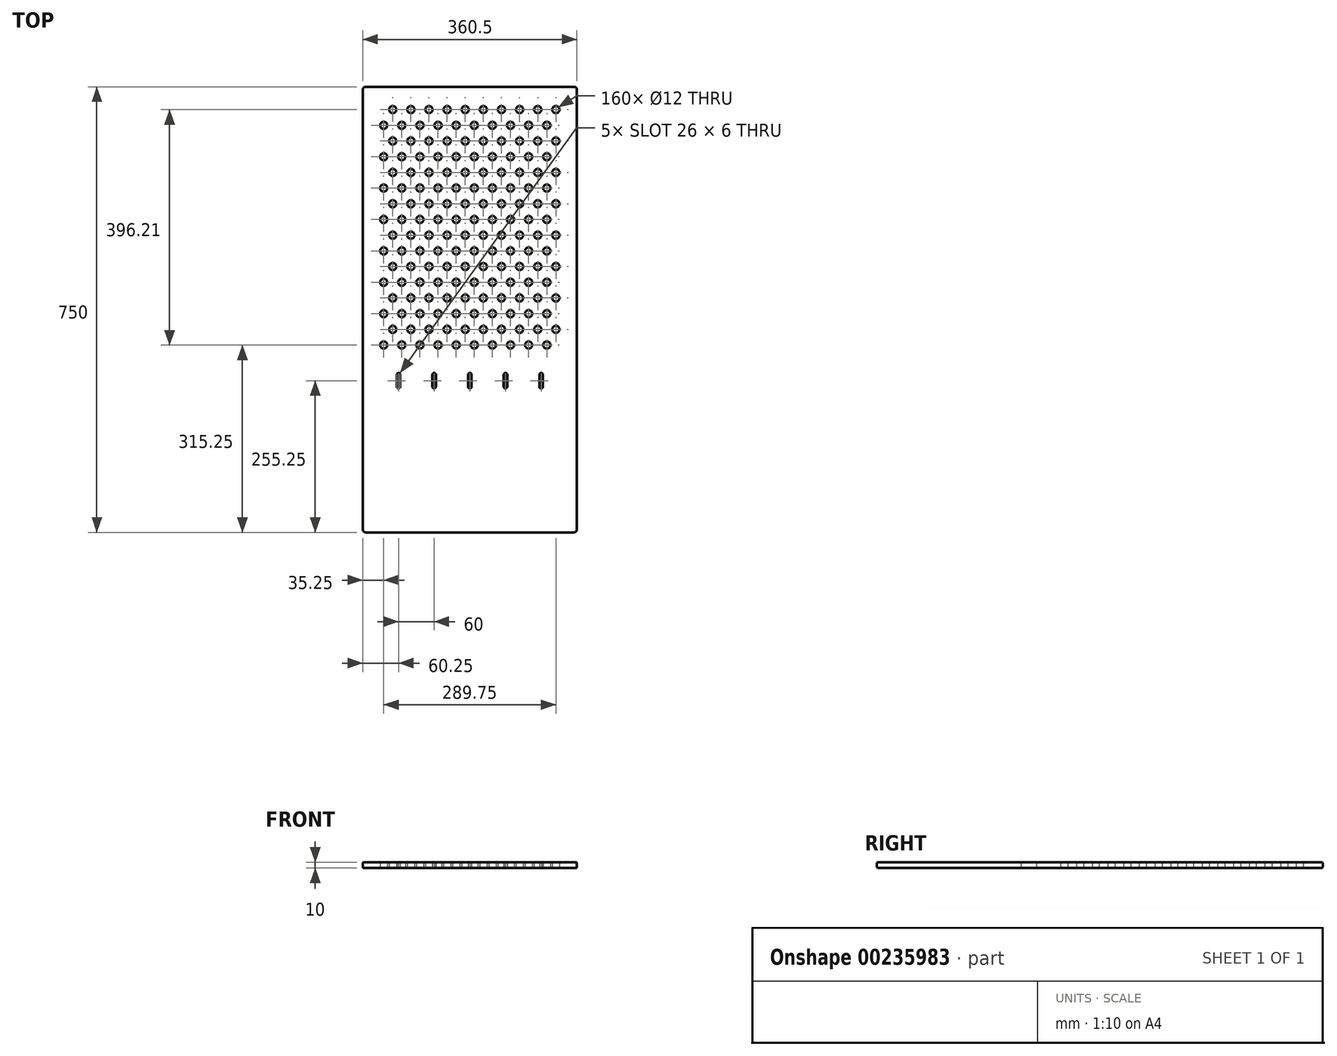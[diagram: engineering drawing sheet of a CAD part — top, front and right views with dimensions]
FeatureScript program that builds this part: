
annotation { "Feature Type Name" : "Feature", "Feature Type Description" : "" }
export const myFeature = defineFeature(function(context is Context, id is Id, definition is map)
    precondition{}
    {
        {
            var Q0;
            Q0=qCreatedBy(makeId("Top.planeOp"),FACE);
            var sketch = newSketch(context, id + "F0", { "sketchPlane" : qUnion([Q0])});
            skCircle(sketch, "E0", {"center": v(0, 0) * mm, "radius": 15.25 * mm, "construction": true});
            skLineSegment(sketch, "E1", {"start": v(-15.25, 59.88) * mm, "end": v(-15.25, -39.27) * mm, "construction": true});
            skLineSegment(sketch, "E2", {"start": v(-42.71, -15.25) * mm, "end": v(49.2, -15.25) * mm, "construction": true});
            skLineSegment(sketch, "E3.direction1", {"start": v(0, 0) * mm, "end": v(30.5, 0) * mm, "construction": true});
            skLineSegment(sketch, "E3.direction2", {"start": v(0, 0) * mm, "end": v(0, 30.5) * mm, "construction": true});
            skCircle(sketch, "E4", {"center": v(0, 0) * mm, "radius": 6 * mm});
            skCircle(sketch, "E5.0.1.0", {"center": v(0, 52.83) * mm, "radius": 6 * mm});
            skCircle(sketch, "E5.0.2.0", {"center": v(0, 105.66) * mm, "radius": 6 * mm});
            skCircle(sketch, "E5.0.3.0", {"center": v(0, 158.48) * mm, "radius": 6 * mm});
            skCircle(sketch, "E5.0.4.0", {"center": v(0, 211.31) * mm, "radius": 6 * mm});
            skCircle(sketch, "E5.0.5.0", {"center": v(0, 264.14) * mm, "radius": 6 * mm});
            skCircle(sketch, "E5.1.0.0", {"center": v(30.5, 0) * mm, "radius": 6 * mm});
            skCircle(sketch, "E5.1.1.0", {"center": v(30.5, 52.83) * mm, "radius": 6 * mm});
            skCircle(sketch, "E5.1.2.0", {"center": v(30.5, 105.66) * mm, "radius": 6 * mm});
            skCircle(sketch, "E5.1.3.0", {"center": v(30.5, 158.48) * mm, "radius": 6 * mm});
            skCircle(sketch, "E5.1.4.0", {"center": v(30.5, 211.31) * mm, "radius": 6 * mm});
            skCircle(sketch, "E5.1.5.0", {"center": v(30.5, 264.14) * mm, "radius": 6 * mm});
            skCircle(sketch, "E5.2.0.0", {"center": v(61, 0) * mm, "radius": 6 * mm});
            skCircle(sketch, "E5.2.1.0", {"center": v(61, 52.83) * mm, "radius": 6 * mm});
            skCircle(sketch, "E5.2.2.0", {"center": v(61, 105.66) * mm, "radius": 6 * mm});
            skCircle(sketch, "E5.2.3.0", {"center": v(61, 158.48) * mm, "radius": 6 * mm});
            skCircle(sketch, "E5.2.4.0", {"center": v(61, 211.31) * mm, "radius": 6 * mm});
            skCircle(sketch, "E5.2.5.0", {"center": v(61, 264.14) * mm, "radius": 6 * mm});
            skCircle(sketch, "E5.3.0.0", {"center": v(91.5, 0) * mm, "radius": 6 * mm});
            skCircle(sketch, "E5.3.1.0", {"center": v(91.5, 52.83) * mm, "radius": 6 * mm});
            skCircle(sketch, "E5.3.2.0", {"center": v(91.5, 105.66) * mm, "radius": 6 * mm});
            skCircle(sketch, "E5.3.3.0", {"center": v(91.5, 158.48) * mm, "radius": 6 * mm});
            skCircle(sketch, "E5.3.4.0", {"center": v(91.5, 211.31) * mm, "radius": 6 * mm});
            skCircle(sketch, "E5.3.5.0", {"center": v(91.5, 264.14) * mm, "radius": 6 * mm});
            skCircle(sketch, "E5.4.0.0", {"center": v(122, 0) * mm, "radius": 6 * mm});
            skCircle(sketch, "E5.4.1.0", {"center": v(122, 52.83) * mm, "radius": 6 * mm});
            skCircle(sketch, "E5.4.2.0", {"center": v(122, 105.66) * mm, "radius": 6 * mm});
            skCircle(sketch, "E5.4.3.0", {"center": v(122, 158.48) * mm, "radius": 6 * mm});
            skCircle(sketch, "E5.4.4.0", {"center": v(122, 211.31) * mm, "radius": 6 * mm});
            skCircle(sketch, "E5.4.5.0", {"center": v(122, 264.14) * mm, "radius": 6 * mm});
            skCircle(sketch, "E5.5.0.0", {"center": v(152.5, 0) * mm, "radius": 6 * mm});
            skCircle(sketch, "E5.5.1.0", {"center": v(152.5, 52.83) * mm, "radius": 6 * mm});
            skCircle(sketch, "E5.5.2.0", {"center": v(152.5, 105.66) * mm, "radius": 6 * mm});
            skCircle(sketch, "E5.5.3.0", {"center": v(152.5, 158.48) * mm, "radius": 6 * mm});
            skCircle(sketch, "E5.5.4.0", {"center": v(152.5, 211.31) * mm, "radius": 6 * mm});
            skCircle(sketch, "E5.5.5.0", {"center": v(152.5, 264.14) * mm, "radius": 6 * mm});
            skCircle(sketch, "E5.6.0.0", {"center": v(183, 0) * mm, "radius": 6 * mm});
            skCircle(sketch, "E5.6.1.0", {"center": v(183, 52.83) * mm, "radius": 6 * mm});
            skCircle(sketch, "E5.6.2.0", {"center": v(183, 105.66) * mm, "radius": 6 * mm});
            skCircle(sketch, "E5.6.3.0", {"center": v(183, 158.48) * mm, "radius": 6 * mm});
            skCircle(sketch, "E5.6.4.0", {"center": v(183, 211.31) * mm, "radius": 6 * mm});
            skCircle(sketch, "E5.6.5.0", {"center": v(183, 264.14) * mm, "radius": 6 * mm});
            skLineSegment(sketch, "E5.direction2", {"start": v(0, 0) * mm, "end": v(0, 52.83) * mm, "construction": true});
            skLineSegment(sketch, "E6", {"start": v(-15.25, -15.25) * mm, "end": v(305.25, -15.25) * mm, "construction": true});
            skPoint(sketch, "E6.endSnap0", {"position": v(3.24, -15.25) * mm});
            skLineSegment(sketch, "E7", {"start": v(305.25, -15.25) * mm, "end": v(305.25, 414.75) * mm, "construction": true});
            skLineSegment(sketch, "E8", {"start": v(305.25, 414.75) * mm, "end": v(-15.25, 414.75) * mm, "construction": true});
            skLineSegment(sketch, "E9", {"start": v(-15.25, 414.75) * mm, "end": v(-15.25, -15.25) * mm, "construction": true});
            skCircle(sketch, "E10.0.7.0", {"center": v(213.5, 0) * mm, "radius": 6 * mm});
            skCircle(sketch, "E10.0.7.1", {"center": v(213.5, 52.83) * mm, "radius": 6 * mm});
            skCircle(sketch, "E10.0.7.2", {"center": v(213.5, 105.66) * mm, "radius": 6 * mm});
            skCircle(sketch, "E10.0.7.3", {"center": v(213.5, 158.48) * mm, "radius": 6 * mm});
            skCircle(sketch, "E10.0.7.4", {"center": v(213.5, 211.31) * mm, "radius": 6 * mm});
            skCircle(sketch, "E10.0.7.5", {"center": v(213.5, 264.14) * mm, "radius": 6 * mm});
            skCircle(sketch, "E10.0.8.0", {"center": v(244, 0) * mm, "radius": 6 * mm});
            skCircle(sketch, "E10.0.8.1", {"center": v(244, 52.83) * mm, "radius": 6 * mm});
            skCircle(sketch, "E10.0.8.2", {"center": v(244, 105.66) * mm, "radius": 6 * mm});
            skCircle(sketch, "E10.0.8.3", {"center": v(244, 158.48) * mm, "radius": 6 * mm});
            skCircle(sketch, "E10.0.8.4", {"center": v(244, 211.31) * mm, "radius": 6 * mm});
            skCircle(sketch, "E10.0.8.5", {"center": v(244, 264.14) * mm, "radius": 6 * mm});
            skCircle(sketch, "E11.0.9.0", {"center": v(274.5, 0) * mm, "radius": 6 * mm});
            skCircle(sketch, "E11.0.9.1", {"center": v(274.5, 52.83) * mm, "radius": 6 * mm});
            skCircle(sketch, "E11.0.9.2", {"center": v(274.5, 105.66) * mm, "radius": 6 * mm});
            skCircle(sketch, "E11.0.9.3", {"center": v(274.5, 158.48) * mm, "radius": 6 * mm});
            skCircle(sketch, "E11.0.9.4", {"center": v(274.5, 211.31) * mm, "radius": 6 * mm});
            skCircle(sketch, "E11.0.9.5", {"center": v(274.5, 264.14) * mm, "radius": 6 * mm});
            skLineSegment(sketch, "E12", {"start": v(-35.25, 434.75) * mm, "end": v(325.25, 434.75) * mm});
            skLineSegment(sketch, "E13", {"start": v(325.25, 434.75) * mm, "end": v(325.25, -315.25) * mm});
            skLineSegment(sketch, "E14", {"start": v(325.25, -315.25) * mm, "end": v(-35.25, -315.25) * mm});
            skLineSegment(sketch, "E15", {"start": v(-35.25, -315.25) * mm, "end": v(-35.25, 434.75) * mm});
            skCircle(sketch, "E16", {"center": v(30.5, 0) * mm, "radius": 15.25 * mm, "construction": true});
            skCircle(sketch, "E17", {"center": v(15.25, 26.41) * mm, "radius": 15.25 * mm, "construction": true});
            skCircle(sketch, "E18", {"center": v(0, 52.83) * mm, "radius": 15.25 * mm, "construction": true});
            skCircle(sketch, "E19.0.0.6", {"center": v(0, 316.97) * mm, "radius": 6 * mm});
            skCircle(sketch, "E19.0.0.7", {"center": v(0, 369.8) * mm, "radius": 6 * mm});
            skCircle(sketch, "E19.0.1.6", {"center": v(30.5, 316.97) * mm, "radius": 6 * mm});
            skCircle(sketch, "E19.0.1.7", {"center": v(30.5, 369.8) * mm, "radius": 6 * mm});
            skCircle(sketch, "E19.0.2.6", {"center": v(61, 316.97) * mm, "radius": 6 * mm});
            skCircle(sketch, "E19.0.2.7", {"center": v(61, 369.8) * mm, "radius": 6 * mm});
            skCircle(sketch, "E19.0.3.6", {"center": v(91.5, 316.97) * mm, "radius": 6 * mm});
            skCircle(sketch, "E19.0.3.7", {"center": v(91.5, 369.8) * mm, "radius": 6 * mm});
            skCircle(sketch, "E19.0.4.6", {"center": v(122, 316.97) * mm, "radius": 6 * mm});
            skCircle(sketch, "E19.0.4.7", {"center": v(122, 369.8) * mm, "radius": 6 * mm});
            skCircle(sketch, "E19.0.5.6", {"center": v(152.5, 316.97) * mm, "radius": 6 * mm});
            skCircle(sketch, "E19.0.5.7", {"center": v(152.5, 369.8) * mm, "radius": 6 * mm});
            skCircle(sketch, "E19.0.6.6", {"center": v(183, 316.97) * mm, "radius": 6 * mm});
            skCircle(sketch, "E19.0.6.7", {"center": v(183, 369.8) * mm, "radius": 6 * mm});
            skCircle(sketch, "E19.0.7.6", {"center": v(213.5, 316.97) * mm, "radius": 6 * mm});
            skCircle(sketch, "E19.0.7.7", {"center": v(213.5, 369.8) * mm, "radius": 6 * mm});
            skCircle(sketch, "E19.0.8.6", {"center": v(244, 316.97) * mm, "radius": 6 * mm});
            skCircle(sketch, "E19.0.8.7", {"center": v(244, 369.8) * mm, "radius": 6 * mm});
            skCircle(sketch, "E19.0.9.6", {"center": v(274.5, 316.97) * mm, "radius": 6 * mm});
            skCircle(sketch, "E19.0.9.7", {"center": v(274.5, 369.8) * mm, "radius": 6 * mm});
            skCircle(sketch, "E20", {"center": v(15.25, 26.41) * mm, "radius": 6 * mm});
            skCircle(sketch, "E21.0.1.0", {"center": v(15.25, 79.24) * mm, "radius": 6 * mm});
            skCircle(sketch, "E21.0.2.0", {"center": v(15.25, 132.07) * mm, "radius": 6 * mm});
            skCircle(sketch, "E21.0.3.0", {"center": v(15.25, 184.9) * mm, "radius": 6 * mm});
            skCircle(sketch, "E21.0.4.0", {"center": v(15.25, 237.73) * mm, "radius": 6 * mm});
            skCircle(sketch, "E21.0.5.0", {"center": v(15.25, 290.55) * mm, "radius": 6 * mm});
            skCircle(sketch, "E21.0.6.0", {"center": v(15.25, 343.38) * mm, "radius": 6 * mm});
            skCircle(sketch, "E21.1.0.0", {"center": v(45.75, 26.41) * mm, "radius": 6 * mm});
            skCircle(sketch, "E21.1.1.0", {"center": v(45.75, 79.24) * mm, "radius": 6 * mm});
            skCircle(sketch, "E21.1.2.0", {"center": v(45.75, 132.07) * mm, "radius": 6 * mm});
            skCircle(sketch, "E21.1.3.0", {"center": v(45.75, 184.9) * mm, "radius": 6 * mm});
            skCircle(sketch, "E21.1.4.0", {"center": v(45.75, 237.73) * mm, "radius": 6 * mm});
            skCircle(sketch, "E21.1.5.0", {"center": v(45.75, 290.55) * mm, "radius": 6 * mm});
            skCircle(sketch, "E21.1.6.0", {"center": v(45.75, 343.38) * mm, "radius": 6 * mm});
            skCircle(sketch, "E21.2.0.0", {"center": v(76.25, 26.41) * mm, "radius": 6 * mm});
            skCircle(sketch, "E21.2.1.0", {"center": v(76.25, 79.24) * mm, "radius": 6 * mm});
            skCircle(sketch, "E21.2.2.0", {"center": v(76.25, 132.07) * mm, "radius": 6 * mm});
            skCircle(sketch, "E21.2.3.0", {"center": v(76.25, 184.9) * mm, "radius": 6 * mm});
            skCircle(sketch, "E21.2.4.0", {"center": v(76.25, 237.73) * mm, "radius": 6 * mm});
            skCircle(sketch, "E21.2.5.0", {"center": v(76.25, 290.55) * mm, "radius": 6 * mm});
            skCircle(sketch, "E21.2.6.0", {"center": v(76.25, 343.38) * mm, "radius": 6 * mm});
            skCircle(sketch, "E21.3.0.0", {"center": v(106.75, 26.41) * mm, "radius": 6 * mm});
            skCircle(sketch, "E21.3.1.0", {"center": v(106.75, 79.24) * mm, "radius": 6 * mm});
            skCircle(sketch, "E21.3.2.0", {"center": v(106.75, 132.07) * mm, "radius": 6 * mm});
            skCircle(sketch, "E21.3.3.0", {"center": v(106.75, 184.9) * mm, "radius": 6 * mm});
            skCircle(sketch, "E21.3.4.0", {"center": v(106.75, 237.73) * mm, "radius": 6 * mm});
            skCircle(sketch, "E21.3.5.0", {"center": v(106.75, 290.55) * mm, "radius": 6 * mm});
            skCircle(sketch, "E21.3.6.0", {"center": v(106.75, 343.38) * mm, "radius": 6 * mm});
            skCircle(sketch, "E21.4.0.0", {"center": v(137.25, 26.41) * mm, "radius": 6 * mm});
            skCircle(sketch, "E21.4.1.0", {"center": v(137.25, 79.24) * mm, "radius": 6 * mm});
            skCircle(sketch, "E21.4.2.0", {"center": v(137.25, 132.07) * mm, "radius": 6 * mm});
            skCircle(sketch, "E21.4.3.0", {"center": v(137.25, 184.9) * mm, "radius": 6 * mm});
            skCircle(sketch, "E21.4.4.0", {"center": v(137.25, 237.73) * mm, "radius": 6 * mm});
            skCircle(sketch, "E21.4.5.0", {"center": v(137.25, 290.55) * mm, "radius": 6 * mm});
            skCircle(sketch, "E21.4.6.0", {"center": v(137.25, 343.38) * mm, "radius": 6 * mm});
            skCircle(sketch, "E21.5.0.0", {"center": v(167.75, 26.41) * mm, "radius": 6 * mm});
            skCircle(sketch, "E21.5.1.0", {"center": v(167.75, 79.24) * mm, "radius": 6 * mm});
            skCircle(sketch, "E21.5.2.0", {"center": v(167.75, 132.07) * mm, "radius": 6 * mm});
            skCircle(sketch, "E21.5.3.0", {"center": v(167.75, 184.9) * mm, "radius": 6 * mm});
            skCircle(sketch, "E21.5.4.0", {"center": v(167.75, 237.73) * mm, "radius": 6 * mm});
            skCircle(sketch, "E21.5.5.0", {"center": v(167.75, 290.55) * mm, "radius": 6 * mm});
            skCircle(sketch, "E21.5.6.0", {"center": v(167.75, 343.38) * mm, "radius": 6 * mm});
            skCircle(sketch, "E21.6.0.0", {"center": v(198.25, 26.41) * mm, "radius": 6 * mm});
            skCircle(sketch, "E21.6.1.0", {"center": v(198.25, 79.24) * mm, "radius": 6 * mm});
            skCircle(sketch, "E21.6.2.0", {"center": v(198.25, 132.07) * mm, "radius": 6 * mm});
            skCircle(sketch, "E21.6.3.0", {"center": v(198.25, 184.9) * mm, "radius": 6 * mm});
            skCircle(sketch, "E21.6.4.0", {"center": v(198.25, 237.73) * mm, "radius": 6 * mm});
            skCircle(sketch, "E21.6.5.0", {"center": v(198.25, 290.55) * mm, "radius": 6 * mm});
            skCircle(sketch, "E21.6.6.0", {"center": v(198.25, 343.38) * mm, "radius": 6 * mm});
            skCircle(sketch, "E21.7.0.0", {"center": v(228.75, 26.41) * mm, "radius": 6 * mm});
            skCircle(sketch, "E21.7.1.0", {"center": v(228.75, 79.24) * mm, "radius": 6 * mm});
            skCircle(sketch, "E21.7.2.0", {"center": v(228.75, 132.07) * mm, "radius": 6 * mm});
            skCircle(sketch, "E21.7.3.0", {"center": v(228.75, 184.9) * mm, "radius": 6 * mm});
            skCircle(sketch, "E21.7.4.0", {"center": v(228.75, 237.73) * mm, "radius": 6 * mm});
            skCircle(sketch, "E21.7.5.0", {"center": v(228.75, 290.55) * mm, "radius": 6 * mm});
            skCircle(sketch, "E21.7.6.0", {"center": v(228.75, 343.38) * mm, "radius": 6 * mm});
            skCircle(sketch, "E21.8.0.0", {"center": v(259.25, 26.41) * mm, "radius": 6 * mm});
            skCircle(sketch, "E21.8.1.0", {"center": v(259.25, 79.24) * mm, "radius": 6 * mm});
            skCircle(sketch, "E21.8.2.0", {"center": v(259.25, 132.07) * mm, "radius": 6 * mm});
            skCircle(sketch, "E21.8.3.0", {"center": v(259.25, 184.9) * mm, "radius": 6 * mm});
            skCircle(sketch, "E21.8.4.0", {"center": v(259.25, 237.73) * mm, "radius": 6 * mm});
            skCircle(sketch, "E21.8.5.0", {"center": v(259.25, 290.55) * mm, "radius": 6 * mm});
            skCircle(sketch, "E21.8.6.0", {"center": v(259.25, 343.38) * mm, "radius": 6 * mm});
            skCircle(sketch, "E21.9.0.0", {"center": v(289.75, 26.41) * mm, "radius": 6 * mm});
            skCircle(sketch, "E21.9.1.0", {"center": v(289.75, 79.24) * mm, "radius": 6 * mm});
            skCircle(sketch, "E21.9.2.0", {"center": v(289.75, 132.07) * mm, "radius": 6 * mm});
            skCircle(sketch, "E21.9.3.0", {"center": v(289.75, 184.9) * mm, "radius": 6 * mm});
            skCircle(sketch, "E21.9.4.0", {"center": v(289.75, 237.73) * mm, "radius": 6 * mm});
            skCircle(sketch, "E21.9.5.0", {"center": v(289.75, 290.55) * mm, "radius": 6 * mm});
            skCircle(sketch, "E21.9.6.0", {"center": v(289.75, 343.38) * mm, "radius": 6 * mm});
            skLineSegment(sketch, "E21.direction1", {"start": v(15.25, 26.41) * mm, "end": v(45.75, 26.41) * mm, "construction": true});
            skLineSegment(sketch, "E21.direction2", {"start": v(15.25, 26.41) * mm, "end": v(15.25, 79.24) * mm, "construction": true});
            skCircle(sketch, "E22.0.0.7", {"center": v(15.25, 396.2) * mm, "radius": 6 * mm});
            skCircle(sketch, "E22.0.1.7", {"center": v(45.75, 396.2) * mm, "radius": 6 * mm});
            skCircle(sketch, "E22.0.2.7", {"center": v(76.25, 396.2) * mm, "radius": 6 * mm});
            skCircle(sketch, "E22.0.3.7", {"center": v(106.75, 396.2) * mm, "radius": 6 * mm});
            skCircle(sketch, "E22.0.4.7", {"center": v(137.25, 396.2) * mm, "radius": 6 * mm});
            skCircle(sketch, "E22.0.5.7", {"center": v(167.75, 396.2) * mm, "radius": 6 * mm});
            skCircle(sketch, "E22.0.6.7", {"center": v(198.25, 396.2) * mm, "radius": 6 * mm});
            skCircle(sketch, "E22.0.7.7", {"center": v(228.75, 396.2) * mm, "radius": 6 * mm});
            skCircle(sketch, "E22.0.8.7", {"center": v(259.25, 396.2) * mm, "radius": 6 * mm});
            skCircle(sketch, "E22.0.9.7", {"center": v(289.75, 396.2) * mm, "radius": 6 * mm});
            skSolve(sketch);
        }
        {
            var Q0;
            Q0 = qSketchRegion(id + "F0", true);
            extrude(context, id + "F1", {"entities" : qUnion([Q0]), "depth" : 10 * mm});
        }
        {
            var Q0;
            Q0=makeQuery(id+"F0.imprint","IMPRINT",FACE,{"disambiguationData":[TD([[makeQuery(id+"F0.imprint","IMPRINT",EDGE,{"derivedFrom":sQuery(id+"F0.wireOp",EDGE,"E4")}),-1.0]])]});
            var sketch = newSketch(context, id + "F2", { "sketchPlane" : qUnion([Q0])});
            skCircle(sketch, "E23", {"center": v(25, -50) * mm, "radius": 3 * mm});
            skLineSegment(sketch, "E24.0", {"start": v(-35.25, -315.25) * mm, "end": v(-35.25, 434.75) * mm});
            skLineSegment(sketch, "E25.0", {"start": v(325.25, 434.75) * mm, "end": v(325.25, -315.25) * mm});
            skLineSegment(sketch, "E26", {"start": v(25, -50) * mm, "end": v(-35.25, -50) * mm, "construction": true});
            skCircle(sketch, "E27.1.0.0", {"center": v(85, -50) * mm, "radius": 3 * mm});
            skCircle(sketch, "E27.2.0.0", {"center": v(145, -50) * mm, "radius": 3 * mm});
            skCircle(sketch, "E27.3.0.0", {"center": v(205, -50) * mm, "radius": 3 * mm});
            skCircle(sketch, "E27.4.0.0", {"center": v(265, -50) * mm, "radius": 3 * mm});
            skLineSegment(sketch, "E27.direction1", {"start": v(25, -50) * mm, "end": v(85, -50) * mm, "construction": true});
            skLineSegment(sketch, "E28", {"start": v(265, -50) * mm, "end": v(325.25, -50) * mm, "construction": true});
            skCircle(sketch, "E29", {"center": v(25, -70) * mm, "radius": 3 * mm});
            skLineSegment(sketch, "E30", {"start": v(22, -70) * mm, "end": v(22, -50) * mm});
            skLineSegment(sketch, "E31", {"start": v(28, -70) * mm, "end": v(28, -50) * mm});
            skCircle(sketch, "E32.1.0.0", {"center": v(85, -70) * mm, "radius": 3 * mm});
            skLineSegment(sketch, "E32.1.0.1", {"start": v(82, -70) * mm, "end": v(82, -50) * mm});
            skLineSegment(sketch, "E32.1.0.2", {"start": v(88, -70) * mm, "end": v(88, -50) * mm});
            skCircle(sketch, "E32.2.0.0", {"center": v(145, -70) * mm, "radius": 3 * mm});
            skLineSegment(sketch, "E32.2.0.1", {"start": v(142, -70) * mm, "end": v(142, -50) * mm});
            skLineSegment(sketch, "E32.2.0.2", {"start": v(148, -70) * mm, "end": v(148, -50) * mm});
            skCircle(sketch, "E32.3.0.0", {"center": v(205, -70) * mm, "radius": 3 * mm});
            skLineSegment(sketch, "E32.3.0.1", {"start": v(202, -70) * mm, "end": v(202, -50) * mm});
            skLineSegment(sketch, "E32.3.0.2", {"start": v(208, -70) * mm, "end": v(208, -50) * mm});
            skCircle(sketch, "E32.4.0.0", {"center": v(265, -70) * mm, "radius": 3 * mm});
            skLineSegment(sketch, "E32.4.0.1", {"start": v(262, -70) * mm, "end": v(262, -50) * mm});
            skLineSegment(sketch, "E32.4.0.2", {"start": v(268, -70) * mm, "end": v(268, -50) * mm});
            skLineSegment(sketch, "E32.direction1", {"start": v(25, -70) * mm, "end": v(85, -70) * mm, "construction": true});
            skSolve(sketch);
        }
        {
            var Q0;
            Q0=makeQuery(id+"F2.imprint","IMPRINT",FACE,{"disambiguationData":[TD([[makeQuery(id+"F2.imprint","IMPRINT",EDGE,{"derivedFrom":sQuery(id+"F2.wireOp",EDGE,"E23")}),1.0]])]});
            var Q1;
            Q1=makeQuery(id+"F2.imprint","IMPRINT",FACE,{"disambiguationData":[TD([[makeQuery(id+"F2.imprint","IMPRINT",EDGE,{"derivedFrom":sQuery(id+"F2.wireOp",EDGE,"E27.1.0.0")}),1.0]])]});
            var Q2;
            Q2=makeQuery(id+"F2.imprint","IMPRINT",FACE,{"disambiguationData":[TD([[makeQuery(id+"F2.imprint","IMPRINT",EDGE,{"derivedFrom":sQuery(id+"F2.wireOp",EDGE,"E27.3.0.0")}),1.0]])]});
            var Q3;
            Q3=makeQuery(id+"F2.imprint","IMPRINT",FACE,{"disambiguationData":[TD([[makeQuery(id+"F2.imprint","IMPRINT",EDGE,{"derivedFrom":sQuery(id+"F2.wireOp",EDGE,"E27.2.0.0")}),1.0]])]});
            var Q4;
            Q4=makeQuery(id+"F2.imprint","IMPRINT",FACE,{"disambiguationData":[TD([[makeQuery(id+"F2.imprint","IMPRINT",EDGE,{"derivedFrom":sQuery(id+"F2.wireOp",EDGE,"E27.4.0.0")}),1.0]])]});
            var Q5;
            {var subQ0=sQuery(id+"F2.wireOp",EDGE,"E30");Q5=makeQuery(id+"F2.imprint","IMPRINT",FACE,{"disambiguationData":[TD([[makeQuery(id+"F2.imprint","IMPRINT",EDGE,{"derivedFrom":subQ0}),-1.0]])]});}
            var Q6;
            {var subQ0=sQuery(id+"F2.wireOp",EDGE,"E29");var subQ1=makeQuery(id+"F2.imprint","INTERSECT",VERTEX,{"derivedFrom":[subQ0,sQuery(id+"F2.wireOp",EDGE,"E30")]});Q6=makeQuery(id+"F2.imprint","IMPRINT",FACE,{"disambiguationData":[TD([[makeQuery(id+"F2.imprint","IMPRINT",EDGE,{"disambiguationData":[TD([[subQ1,1.0]])],"derivedFrom":subQ0}),1.0]])]});}
            var Q7;
            {var subQ0=sQuery(id+"F2.wireOp",EDGE,"E32.1.0.1");Q7=makeQuery(id+"F2.imprint","IMPRINT",FACE,{"disambiguationData":[TD([[makeQuery(id+"F2.imprint","IMPRINT",EDGE,{"derivedFrom":subQ0}),-1.0]])]});}
            var Q8;
            {var subQ0=sQuery(id+"F2.wireOp",EDGE,"E32.1.0.0");var subQ1=makeQuery(id+"F2.imprint","INTERSECT",VERTEX,{"derivedFrom":[subQ0,sQuery(id+"F2.wireOp",EDGE,"E32.1.0.1")]});Q8=makeQuery(id+"F2.imprint","IMPRINT",FACE,{"disambiguationData":[TD([[makeQuery(id+"F2.imprint","IMPRINT",EDGE,{"disambiguationData":[TD([[subQ1,1.0]])],"derivedFrom":subQ0}),1.0]])]});}
            var Q9;
            {var subQ0=sQuery(id+"F2.wireOp",EDGE,"E32.2.0.0");var subQ1=makeQuery(id+"F2.imprint","INTERSECT",VERTEX,{"derivedFrom":[subQ0,sQuery(id+"F2.wireOp",EDGE,"E32.2.0.1")]});Q9=makeQuery(id+"F2.imprint","IMPRINT",FACE,{"disambiguationData":[TD([[makeQuery(id+"F2.imprint","IMPRINT",EDGE,{"disambiguationData":[TD([[subQ1,1.0]])],"derivedFrom":subQ0}),1.0]])]});}
            var Q10;
            {var subQ0=sQuery(id+"F2.wireOp",EDGE,"E32.2.0.1");Q10=makeQuery(id+"F2.imprint","IMPRINT",FACE,{"disambiguationData":[TD([[makeQuery(id+"F2.imprint","IMPRINT",EDGE,{"derivedFrom":subQ0}),-1.0]])]});}
            var Q11;
            {var subQ0=sQuery(id+"F2.wireOp",EDGE,"E32.3.0.0");var subQ1=makeQuery(id+"F2.imprint","INTERSECT",VERTEX,{"derivedFrom":[subQ0,sQuery(id+"F2.wireOp",EDGE,"E32.3.0.1")]});Q11=makeQuery(id+"F2.imprint","IMPRINT",FACE,{"disambiguationData":[TD([[makeQuery(id+"F2.imprint","IMPRINT",EDGE,{"disambiguationData":[TD([[subQ1,1.0]])],"derivedFrom":subQ0}),1.0]])]});}
            var Q12;
            {var subQ0=sQuery(id+"F2.wireOp",EDGE,"E32.3.0.1");Q12=makeQuery(id+"F2.imprint","IMPRINT",FACE,{"disambiguationData":[TD([[makeQuery(id+"F2.imprint","IMPRINT",EDGE,{"derivedFrom":subQ0}),-1.0]])]});}
            var Q13;
            {var subQ0=sQuery(id+"F2.wireOp",EDGE,"E32.4.0.1");Q13=makeQuery(id+"F2.imprint","IMPRINT",FACE,{"disambiguationData":[TD([[makeQuery(id+"F2.imprint","IMPRINT",EDGE,{"derivedFrom":subQ0}),-1.0]])]});}
            var Q14;
            {var subQ0=sQuery(id+"F2.wireOp",EDGE,"E32.4.0.0");var subQ1=makeQuery(id+"F2.imprint","INTERSECT",VERTEX,{"derivedFrom":[subQ0,sQuery(id+"F2.wireOp",EDGE,"E32.4.0.1")]});Q14=makeQuery(id+"F2.imprint","IMPRINT",FACE,{"disambiguationData":[TD([[makeQuery(id+"F2.imprint","IMPRINT",EDGE,{"disambiguationData":[TD([[subQ1,1.0]])],"derivedFrom":subQ0}),1.0]])]});}
            extrude(context, id + "F3", {"entities" : qUnion([Q0, Q1, Q2, Q3, Q4, Q5, Q6, Q7, Q8, Q9, Q10, Q11, Q12, Q13, Q14]), "operationType" : NewBodyOperationType.REMOVE, "depth" : 25 * mm});
        }
        {
            var Q0;
            Q0=makeQuery(id+"F1.opExtrude","SWEPT_EDGE",EDGE,{"disambiguationData":[OSD([sQuery(id+"F0.wireOp",EDGE,"E14"),sQuery(id+"F0.wireOp",EDGE,"E15")])]});
            var Q1;
            Q1=makeQuery(id+"F1.opExtrude","SWEPT_EDGE",EDGE,{"disambiguationData":[OSD([sQuery(id+"F0.wireOp",EDGE,"E13"),sQuery(id+"F0.wireOp",EDGE,"E14")])]});
            var Q2;
            Q2=makeQuery(id+"F1.opExtrude","SWEPT_EDGE",EDGE,{"disambiguationData":[OSD([sQuery(id+"F0.wireOp",EDGE,"E12"),sQuery(id+"F0.wireOp",EDGE,"E13")])]});
            var Q3;
            Q3=makeQuery(id+"F1.opExtrude","SWEPT_EDGE",EDGE,{"disambiguationData":[OSD([sQuery(id+"F0.wireOp",EDGE,"E12"),sQuery(id+"F0.wireOp",EDGE,"E15")])]});
            fillet(context, id + "F4", {"entities" : qUnion([Q0, Q1, Q2, Q3]), "radius" : 5 * mm, "tangentPropagation" : true, "allowEdgeOverflow" : false});
        }
        {
            var Q0;
            Q0=makeQuery(id+"F1.opExtrude","CAP_EDGE",EDGE,{"disambiguationData":[OSD([sQuery(id+"F0.wireOp",EDGE,"E14")])],"isStart":false});
            var Q1;
            Q1=makeQuery(id+"F1.opExtrude","CAP_EDGE",EDGE,{"disambiguationData":[OSD([sQuery(id+"F0.wireOp",EDGE,"E14")])],"isStart":true});
            fillet(context, id + "F5", {"entities" : qUnion([Q0, Q1]), "radius" : 2 * mm, "tangentPropagation" : true, "allowEdgeOverflow" : false});
        }
    });
